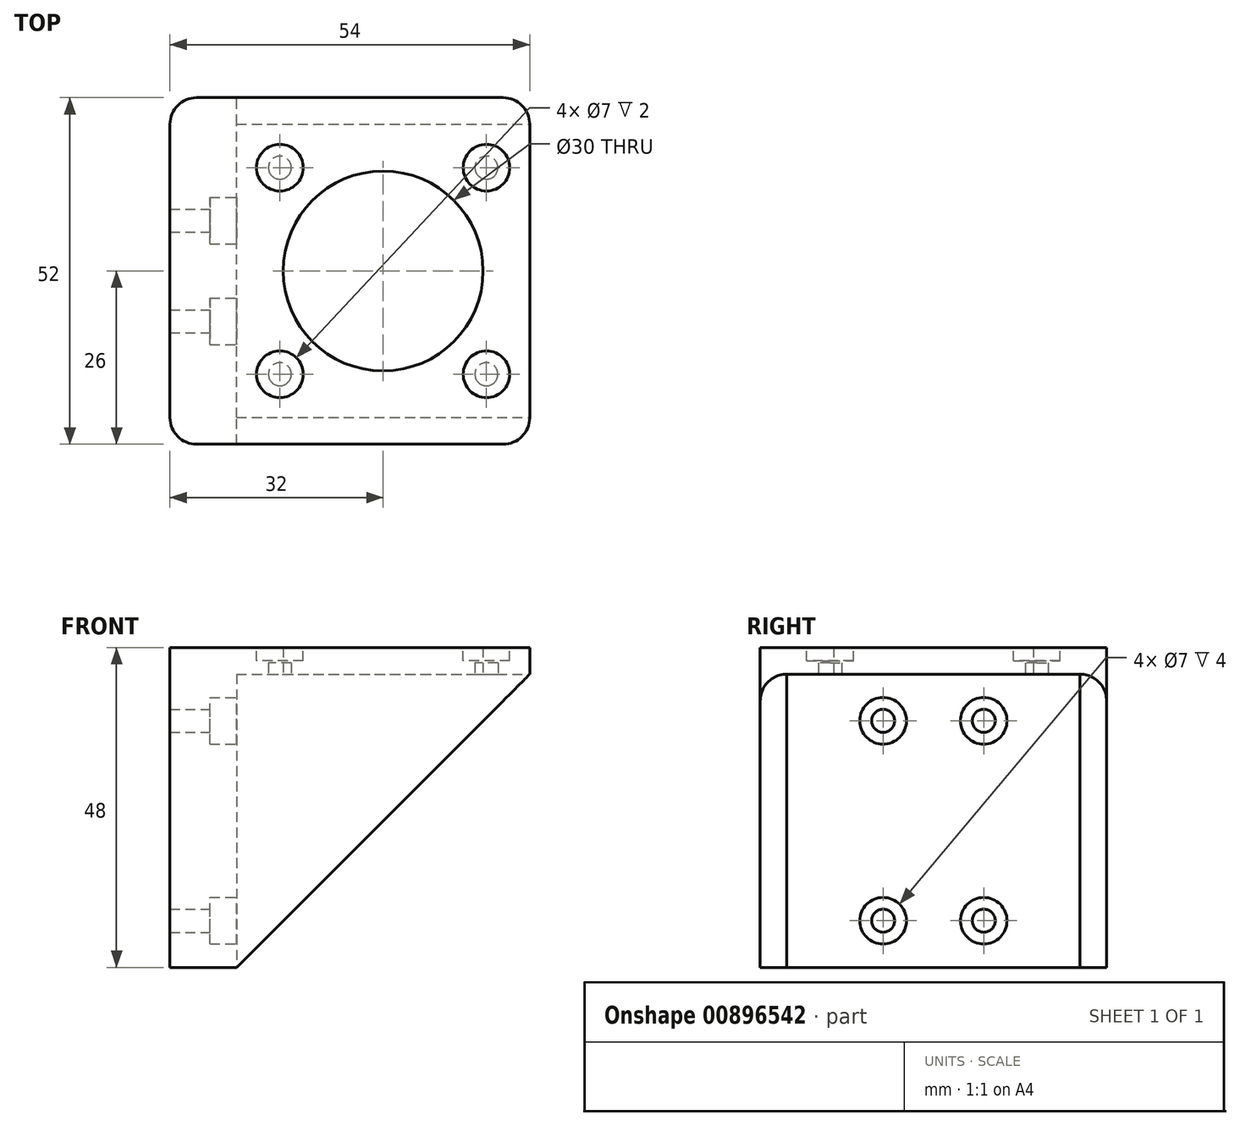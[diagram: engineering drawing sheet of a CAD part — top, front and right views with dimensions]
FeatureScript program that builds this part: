
annotation { "Feature Type Name" : "Feature", "Feature Type Description" : "" }
export const myFeature = defineFeature(function(context is Context, id is Id, definition is map)
    precondition{}
    {
        {
            var Q0;
            Q0=qCreatedBy(makeId("Top.planeOp"),FACE);
            var sketch = newSketch(context, id + "F0", { "sketchPlane" : qUnion([Q0])});
            skLineSegment(sketch, "E0.bottom", {"start": v(0, 0) * mm, "end": v(10, 0) * mm});
            skLineSegment(sketch, "E0.top", {"start": v(0, 52) * mm, "end": v(10, 52) * mm});
            skLineSegment(sketch, "E0.left", {"start": v(0, 0) * mm, "end": v(0, 52) * mm});
            skLineSegment(sketch, "E0.right", {"start": v(10, 0) * mm, "end": v(10, 52) * mm});
            skSolve(sketch);
        }
        {
            var Q0;
            Q0 = qSketchRegion(id + "F0", true);
            extrude(context, id + "F1", {"entities" : qUnion([Q0]), "depth" : 44 * mm, "offsetDistance" : 25 * mm});
        }
        {
            var Q0;
            Q0=makeQuery(id+"F1.opExtrude","CAP_FACE",FACE,{"disambiguationData":[OSD([sQuery(id+"F0.wireOp",EDGE,"E0.bottom"),sQuery(id+"F0.wireOp",EDGE,"E0.top"),sQuery(id+"F0.wireOp",EDGE,"E0.left"),sQuery(id+"F0.wireOp",EDGE,"E0.right")])],"isStart":false});
            var sketch = newSketch(context, id + "F2", { "sketchPlane" : qUnion([Q0])});
            skLineSegment(sketch, "E1.bottom", {"start": v(0, 52) * mm, "end": v(54, 52) * mm});
            skLineSegment(sketch, "E1.top", {"start": v(0, 0) * mm, "end": v(54, 0) * mm});
            skLineSegment(sketch, "E1.left", {"start": v(0, 52) * mm, "end": v(0, 0) * mm});
            skLineSegment(sketch, "E1.right", {"start": v(54, 52) * mm, "end": v(54, 0) * mm});
            skSolve(sketch);
        }
        {
            var Q0;
            Q0 = qSketchRegion(id + "F2", true);
            extrude(context, id + "F3", {"entities" : qUnion([Q0]), "operationType" : NewBodyOperationType.ADD, "depth" : 4 * mm, "offsetDistance" : 25 * mm});
        }
        {
            var Q0;
            Q0=makeQuery(id+"F3.boolean.opBoolean","MERGE",FACE,{"derivedFrom":[makeQuery(id+"F1.opExtrude","SWEPT_FACE",FACE,{"disambiguationData":[OSD([sQuery(id+"F0.wireOp",EDGE,"E0.bottom")])]}),makeQuery(id+"F3.opExtrude","SWEPT_FACE",FACE,{"disambiguationData":[OSD([sQuery(id+"F2.wireOp",EDGE,"E1.top")])]})]});
            var sketch = newSketch(context, id + "F4", { "sketchPlane" : qUnion([Q0])});
            skLineSegment(sketch, "E2", {"start": v(54, 44) * mm, "end": v(10, 0) * mm});
            skLineSegment(sketch, "E3", {"start": v(54, 44) * mm, "end": v(10, 44) * mm});
            skLineSegment(sketch, "E4", {"start": v(10, 44) * mm, "end": v(10, 0) * mm});
            skSolve(sketch);
        }
        {
            var Q0;
            Q0 = qSketchRegion(id + "F4", true);
            extrude(context, id + "F5", {"entities" : qUnion([Q0]), "operationType" : NewBodyOperationType.ADD, "oppositeDirection" : true, "depth" : 4 * mm, "offsetDistance" : 25 * mm});
        }
        {
            var Q0;
            Q0=makeQuery(id+"F3.boolean.opBoolean","MERGE",FACE,{"derivedFrom":[makeQuery(id+"F1.opExtrude","SWEPT_FACE",FACE,{"disambiguationData":[OSD([sQuery(id+"F0.wireOp",EDGE,"E0.top")])]}),makeQuery(id+"F3.opExtrude","SWEPT_FACE",FACE,{"disambiguationData":[OSD([sQuery(id+"F2.wireOp",EDGE,"E1.bottom")])]})]});
            var sketch = newSketch(context, id + "F6", { "sketchPlane" : qUnion([Q0])});
            skLineSegment(sketch, "E5", {"start": v(-54, 44) * mm, "end": v(-10, 0) * mm});
            skLineSegment(sketch, "E6", {"start": v(-10, 0) * mm, "end": v(-10, 44) * mm});
            skLineSegment(sketch, "E7", {"start": v(-10, 44) * mm, "end": v(-54, 44) * mm});
            skSolve(sketch);
        }
        {
            var Q0;
            Q0 = qSketchRegion(id + "F6", true);
            extrude(context, id + "F7", {"entities" : qUnion([Q0]), "operationType" : NewBodyOperationType.ADD, "oppositeDirection" : true, "depth" : 4 * mm, "offsetDistance" : 25 * mm});
        }
        {
            var Q0;
            Q0=makeQuery(id+"F3.opExtrude","CAP_FACE",FACE,{"disambiguationData":[OSD([sQuery(id+"F2.wireOp",EDGE,"E1.bottom"),sQuery(id+"F2.wireOp",EDGE,"E1.top"),sQuery(id+"F2.wireOp",EDGE,"E1.left"),sQuery(id+"F2.wireOp",EDGE,"E1.right")])],"isStart":true});
            var sketch = newSketch(context, id + "F8", { "sketchPlane" : qUnion([Q0])});
            skLineSegment(sketch, "E8", {"start": v(32, -48) * mm, "end": v(32, -26) * mm, "construction": true});
            skLineSegment(sketch, "E9", {"start": v(32, -26) * mm, "end": v(54, -26) * mm, "construction": true});
            skCircle(sketch, "E10", {"center": v(32, -26) * mm, "radius": 15 * mm});
            skLineSegment(sketch, "E11.bottom", {"start": v(16.5, -10.5) * mm, "end": v(47.5, -10.5) * mm, "construction": true});
            skLineSegment(sketch, "E11.top", {"start": v(16.5, -41.5) * mm, "end": v(47.5, -41.5) * mm, "construction": true});
            skLineSegment(sketch, "E11.left", {"start": v(16.5, -10.5) * mm, "end": v(16.5, -41.5) * mm, "construction": true});
            skLineSegment(sketch, "E11.right", {"start": v(47.5, -10.5) * mm, "end": v(47.5, -41.5) * mm, "construction": true});
            skCircle(sketch, "E12", {"center": v(16.5, -10.5) * mm, "radius": 1.73 * mm});
            skCircle(sketch, "E13", {"center": v(47.5, -10.5) * mm, "radius": 1.73 * mm});
            skCircle(sketch, "E14", {"center": v(47.5, -41.5) * mm, "radius": 1.73 * mm});
            skCircle(sketch, "E15", {"center": v(16.5, -41.5) * mm, "radius": 1.73 * mm});
            skSolve(sketch);
        }
        {
            var Q0;
            Q0 = qSketchRegion(id + "F8", true);
            extrude(context, id + "F9", {"entities" : qUnion([Q0]), "operationType" : NewBodyOperationType.REMOVE, "endBound" : BoundingType.UP_TO_NEXT, "oppositeDirection" : true, "depth" : 2 * mm, "offsetDistance" : 25 * mm});
        }
        {
            var Q0;
            Q0=makeQuery(id+"F1.opExtrude","SWEPT_FACE",FACE,{"disambiguationData":[OSD([sQuery(id+"F0.wireOp",EDGE,"E0.right")])]});
            var sketch = newSketch(context, id + "F10", { "sketchPlane" : qUnion([Q0])});
            skLineSegment(sketch, "E16.bottom", {"start": v(18.45, 37) * mm, "end": v(33.55, 37) * mm, "construction": true});
            skLineSegment(sketch, "E16.top", {"start": v(18.45, 7) * mm, "end": v(33.55, 7) * mm, "construction": true});
            skLineSegment(sketch, "E16.left", {"start": v(18.45, 37) * mm, "end": v(18.45, 7) * mm, "construction": true});
            skLineSegment(sketch, "E16.right", {"start": v(33.55, 37) * mm, "end": v(33.55, 7) * mm, "construction": true});
            skLineSegment(sketch, "E17", {"start": v(26, 44) * mm, "end": v(26, 37) * mm, "construction": true});
            skLineSegment(sketch, "E18", {"start": v(48, 22) * mm, "end": v(33.55, 22) * mm, "construction": true});
            skPoint(sketch, "E18.endSnap0", {"position": v(33.55, 22) * mm});
            skCircle(sketch, "E19", {"center": v(18.45, 37) * mm, "radius": 1.73 * mm});
            skCircle(sketch, "E20", {"center": v(33.55, 37) * mm, "radius": 1.73 * mm});
            skCircle(sketch, "E21", {"center": v(33.55, 7) * mm, "radius": 1.73 * mm});
            skCircle(sketch, "E22", {"center": v(18.45, 7) * mm, "radius": 1.73 * mm});
            skCircle(sketch, "E23", {"center": v(18.45, 37) * mm, "radius": 3.5 * mm});
            skCircle(sketch, "E24", {"center": v(33.55, 37) * mm, "radius": 3.5 * mm});
            skCircle(sketch, "E25", {"center": v(33.55, 7) * mm, "radius": 3.5 * mm});
            skCircle(sketch, "E26", {"center": v(18.45, 7) * mm, "radius": 3.5 * mm});
            skSolve(sketch);
        }
        {
            var Q0;
            Q0=makeQuery(id+"F10.imprint","IMPRINT",FACE,{"disambiguationData":[TD([[makeQuery(id+"F10.imprint","IMPRINT",EDGE,{"derivedFrom":sQuery(id+"F10.wireOp",EDGE,"E19")}),1.0]])]});
            var Q1;
            Q1=makeQuery(id+"F10.imprint","IMPRINT",FACE,{"disambiguationData":[TD([[makeQuery(id+"F10.imprint","IMPRINT",EDGE,{"derivedFrom":sQuery(id+"F10.wireOp",EDGE,"E20")}),1.0]])]});
            var Q2;
            Q2=makeQuery(id+"F10.imprint","IMPRINT",FACE,{"disambiguationData":[TD([[makeQuery(id+"F10.imprint","IMPRINT",EDGE,{"derivedFrom":sQuery(id+"F10.wireOp",EDGE,"E21")}),1.0]])]});
            var Q3;
            Q3=makeQuery(id+"F10.imprint","IMPRINT",FACE,{"disambiguationData":[TD([[makeQuery(id+"F10.imprint","IMPRINT",EDGE,{"derivedFrom":sQuery(id+"F10.wireOp",EDGE,"E22")}),1.0]])]});
            extrude(context, id + "F11", {"entities" : qUnion([Q0, Q1, Q2, Q3]), "operationType" : NewBodyOperationType.REMOVE, "oppositeDirection" : true, "depth" : 10 * mm, "offsetDistance" : 25 * mm});
        }
        {
            var Q0;
            Q0 = qSketchRegion(id + "F10", true);
            extrude(context, id + "F12", {"entities" : qUnion([Q0]), "operationType" : NewBodyOperationType.REMOVE, "oppositeDirection" : true, "depth" : 4 * mm, "offsetDistance" : 25 * mm});
        }
        {
            var Q0;
            Q0=makeQuery(id+"F3.boolean.opBoolean","MERGE",EDGE,{"derivedFrom":[makeQuery(id+"F1.opExtrude","SWEPT_EDGE",EDGE,{"disambiguationData":[OSD([sQuery(id+"F0.wireOp",EDGE,"E0.bottom"),sQuery(id+"F0.wireOp",EDGE,"E0.left")])]}),makeQuery(id+"F3.opExtrude","SWEPT_EDGE",EDGE,{"disambiguationData":[OSD([sQuery(id+"F2.wireOp",EDGE,"E1.top"),sQuery(id+"F2.wireOp",EDGE,"E1.left")])]})]});
            var Q1;
            Q1=makeQuery(id+"F3.boolean.opBoolean","MERGE",EDGE,{"derivedFrom":[makeQuery(id+"F1.opExtrude","SWEPT_EDGE",EDGE,{"disambiguationData":[OSD([sQuery(id+"F0.wireOp",EDGE,"E0.top"),sQuery(id+"F0.wireOp",EDGE,"E0.left")])]}),makeQuery(id+"F3.opExtrude","SWEPT_EDGE",EDGE,{"disambiguationData":[OSD([sQuery(id+"F2.wireOp",EDGE,"E1.bottom"),sQuery(id+"F2.wireOp",EDGE,"E1.left")])]})]});
            var Q2;
            Q2=makeQuery(id+"F3.opExtrude","SWEPT_EDGE",EDGE,{"disambiguationData":[OSD([sQuery(id+"F2.wireOp",EDGE,"E1.bottom"),sQuery(id+"F2.wireOp",EDGE,"E1.right")])]});
            var Q3;
            Q3=makeQuery(id+"F3.opExtrude","SWEPT_EDGE",EDGE,{"disambiguationData":[OSD([sQuery(id+"F2.wireOp",EDGE,"E1.top"),sQuery(id+"F2.wireOp",EDGE,"E1.right")])]});
            fillet(context, id + "F13", {"entities" : qUnion([Q0, Q1, Q2, Q3]), "radius" : 4 * mm, "tangentPropagation" : true, "allowEdgeOverflow" : false});
        }
        {
            var Q0;
            Q0=makeQuery(id+"F3.opExtrude","CAP_FACE",FACE,{"disambiguationData":[OSD([sQuery(id+"F2.wireOp",EDGE,"E1.bottom"),sQuery(id+"F2.wireOp",EDGE,"E1.top"),sQuery(id+"F2.wireOp",EDGE,"E1.left"),sQuery(id+"F2.wireOp",EDGE,"E1.right")])],"isStart":false});
            var sketch = newSketch(context, id + "F14", { "sketchPlane" : qUnion([Q0])});
            skCircle(sketch, "E27", {"center": v(16.5, 41.5) * mm, "radius": 3.5 * mm});
            skCircle(sketch, "E28", {"center": v(47.5, 41.5) * mm, "radius": 3.5 * mm});
            skCircle(sketch, "E29", {"center": v(47.5, 10.5) * mm, "radius": 3.5 * mm});
            skCircle(sketch, "E30", {"center": v(16.5, 10.5) * mm, "radius": 3.5 * mm});
            skSolve(sketch);
        }
        {
            var Q0;
            Q0 = qSketchRegion(id + "F14", true);
            extrude(context, id + "F15", {"entities" : qUnion([Q0]), "operationType" : NewBodyOperationType.REMOVE, "oppositeDirection" : true, "depth" : 2 * mm, "offsetDistance" : 25 * mm});
        }
        {
            var Q0;
            Q0=makeQuery(id+"F15.boolean.opBoolean","COPY",FACE,{"derivedFrom":makeQuery(id+"F15.opExtrude","CAP_FACE",FACE,{"disambiguationData":[OSD([sQuery(id+"F14.wireOp",EDGE,"E27")])],"isStart":false})});
            var sketch = newSketch(context, id + "F16", { "sketchPlane" : qUnion([Q0])});
            skCircle(sketch, "E31.0", {"center": v(47.5, 10.5) * mm, "radius": 1.73 * mm});
            skCircle(sketch, "E32.0", {"center": v(47.5, 41.5) * mm, "radius": 1.73 * mm});
            skCircle(sketch, "E33.0", {"center": v(16.5, 10.5) * mm, "radius": 1.73 * mm});
            skCircle(sketch, "E34", {"center": v(16.5, 41.5) * mm, "radius": 1.73 * mm});
            skSolve(sketch);
        }
        {
            var Q0;
            Q0 = qSketchRegion(id + "F16", true);
            extrude(context, id + "F17", {"entities" : qUnion([Q0]), "operationType" : NewBodyOperationType.ADD, "oppositeDirection" : true, "depth" : 0.3 * mm, "offsetDistance" : 25 * mm});
        }
    });
